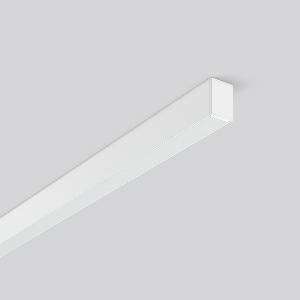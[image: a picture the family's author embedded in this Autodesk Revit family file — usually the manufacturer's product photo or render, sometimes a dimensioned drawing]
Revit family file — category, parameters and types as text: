
# Revit family: less_is_more_27_312198_002_1_76_8459
name_source: partatom
category: Lighting Fixtures
units: mm (PartAtom-declared; Revit-internal decimal feet)

## family parameters
Cut with Voids When Loaded = No
Host = Face
Light Source = No
Part Type = Normal
Room Calculation Point = No
Round Connector Dimension = Use Diameter
Shared = No

## types (1)
- LESS IS MORE 27 (1 x LED Modul 840, 2350 lm, 4000)
    Apparent Load = 31 VA
    CIE Flux Codes = 48 79 96 100 100
    Color Rendering = 80
    Color Temperature = 4000
    Default Elevation = 1800 mm
    Description = Series: LESS IS MORE 27
Ceiling and wall luminaire with slim design. Housing: extruded aluminium profile, powder-coated. End cap aluminium powder-coated. Diffuser made of non-yellowing plastic (PMMA), opal. Suitable for Ceiling mounting, Wall (surface). External driver with connecting cable. 
Colour: traffic white, matt (RAL 9016)
Length: 1212 mm
Width: 28 mm
Height: 38 mm
Lamp: LED
Socket: without socket
Colour temperature: 4000K
Colour rendering index (CRI): 82
System power: 31 W
Rated luminous flux: 2350 lm
Luminous efficiency: 76 lm/W
Control gear: Voltage converter, DALI dim.
Protection class: II
Type of protection: IP 20
    Height = 38 mm
    Lamp = 1 x LED Modul 840
    Lamp Light Flux = 2350 lm
    Lamp count = 1
    Length = 1212 mm
    Lifetime = 50000 h
    Luminous efficacy = 76 lm/W
    Manufacturer = RZB
    ModVariant = No
    Model = 312198.002.1.76
    Mounting Place = Ceiling, Wall
    Mounting Type = Surface mounted
    Number of Poles = 1
    OnlyDefault = Yes
    Power Factor = 1
    Product Name = LESS IS MORE 27
    Product group = Surface mounted LED linear luminaires
    ProductGroupID = 307
    Protection Class = Protection class II
    Protection Degree = IP 20
    RLX_Detail_Level = 1
    RLX_Emergency_Light_Flux = 0 lm
    RLX_Emergency_Type = 0
    RLX_Emergency_Type_DB = No
    RlxData = <blob elided: 22797 chars, md5=6230f993>
    Socket = socket
    Standby Power = 0 W
    System Light Flux = 2350 lm
    System Power = 31 W
    Type Comments = Product without accessories
    Type Image = 312196.002.jpg
    URL = http://relux.com
    VarID = ---
    Voltage = 230 V
    Voltage Range = 220-240 V
    Weight = 0.00 kg
    Width = 28 mm

## geometry (parser evidence)
native form markers: Blend x4, Sweep x12
no freeform markers — native parametric forms only
